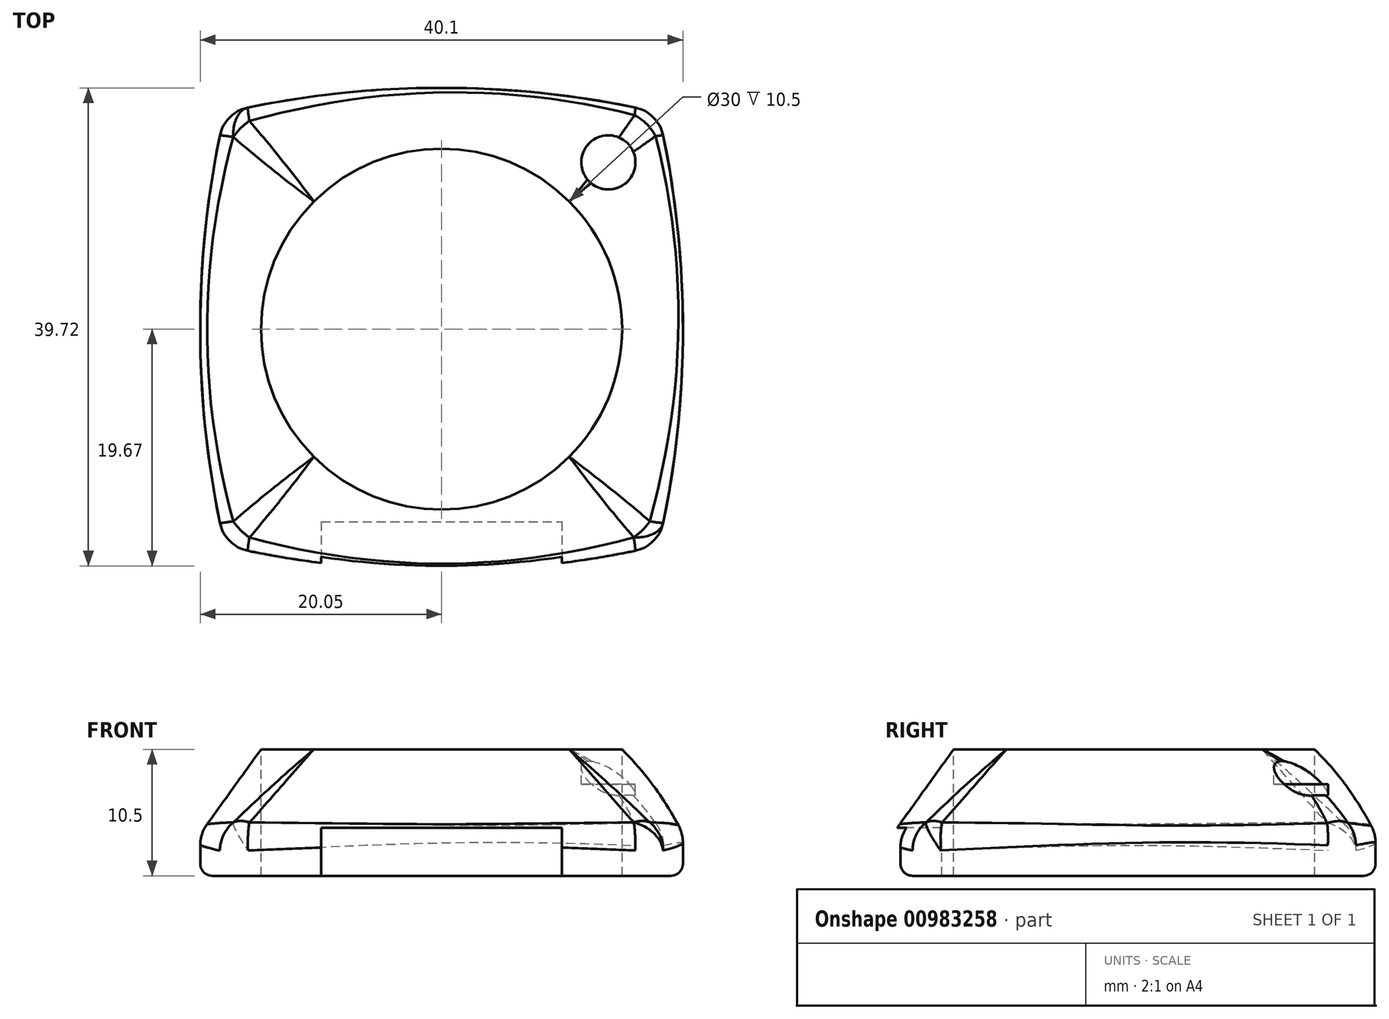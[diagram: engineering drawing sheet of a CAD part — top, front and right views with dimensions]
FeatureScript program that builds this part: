
annotation { "Feature Type Name" : "Feature", "Feature Type Description" : "" }
export const myFeature = defineFeature(function(context is Context, id is Id, definition is map)
    precondition{}
    {
        {
            assignVariable(context, id + "F0", {"name" : "base", "anyValue" : .333});
        }
        {
            assignVariable(context, id + "F1", {"name" : "Height", "anyValue" : 10.5});
        }
        {
            assignVariable(context, id + "F2", {"name" : "depth", "anyValue" : 2.9});
        }
        {
            var Q0;
            Q0=qCreatedBy(makeId("Top.planeOp"),FACE);
            var sketch = newSketch(context, id + "F3", { "sketchPlane" : qUnion([Q0])});
            skLineSegment(sketch, "E0.bottom", {"start": v(18, 18) * mm, "end": v(-18, 18) * mm});
            skLineSegment(sketch, "E0.top", {"start": v(18, -18) * mm, "end": v(-18, -18) * mm});
            skLineSegment(sketch, "E0.left", {"start": v(18, 18) * mm, "end": v(18, -18) * mm});
            skLineSegment(sketch, "E0.right", {"start": v(-18, 18) * mm, "end": v(-18, -18) * mm});
            skPoint(sketch, "E0.middle", {"position": v(0, 0) * mm});
            skArc(sketch, "E1", {"start": v(-18, 18) * mm, "mid": v(-20.05, 0) * mm, "end": v(-18, -18) * mm});
            skArc(sketch, "E2", {"start": v(18, 18) * mm, "mid": v(0, 20.05) * mm, "end": v(-18, 18) * mm});
            skArc(sketch, "E3.MirrorCS", {"start": v(18, -18) * mm, "mid": v(0, -20.05) * mm, "end": v(-18, -18) * mm});
            skArc(sketch, "E4.MirrorCS", {"start": v(18, 18) * mm, "mid": v(20.05, 0) * mm, "end": v(18, -18) * mm});
            skLineSegment(sketch, "E5", {"start": v(-18, 18) * mm, "end": v(18, -18) * mm, "construction": true});
            skLineSegment(sketch, "E6", {"start": v(18, 18) * mm, "end": v(-18, -18) * mm, "construction": true});
            skPoint(sketch, "E7", {"position": v(20.05, 0) * mm});
            skPoint(sketch, "E8", {"position": v(-20.05, 0) * mm});
            skSolve(sketch);
        }
        {
            var Q0;
            Q0=qCreatedBy(makeId("Top.planeOp"),FACE);
            cPlane(context, id + "F4", {"entities" : qUnion([Q0]), "cplaneType" : CPlaneType.OFFSET, "offset" : ((1 - getVariable(context, 'base')) * getVariable(context, 'Height')) * mm, "width" : 150 * mm, "height" : 150 * mm});
        }
        {
            var Q0;
            Q0=qSketchRegion(id+"F3",true);
            extrude(context, id + "F5", {"entities" : qUnion([Q0]), "oppositeDirection" : true, "depth" : (getVariable(context, 'base') * getVariable(context, 'Height')) * mm, "offsetDistance" : 25 * mm});
        }
        {
            var Q0;
            Q0=qCreatedBy(id+"F4.planeOp",FACE);
            var sketch = newSketch(context, id + "F6", { "sketchPlane" : qUnion([Q0])});
            skCircle(sketch, "E9", {"center": v(0, 0) * mm, "radius": 15 * mm});
            skPoint(sketch, "E10", {"position": v(15, 0) * mm});
            skPoint(sketch, "E11.1.0", {"position": v(10.6, 10.6) * mm});
            skPoint(sketch, "E11.2.0", {"position": v(0, 15) * mm});
            skPoint(sketch, "E11.3.0", {"position": v(-10.6, 10.6) * mm});
            skPoint(sketch, "E11.4.0", {"position": v(-15, 0) * mm});
            skPoint(sketch, "E11.5.0", {"position": v(-10.6, -10.6) * mm});
            skPoint(sketch, "E11.6.0", {"position": v(0, -15) * mm});
            skPoint(sketch, "E11.7.0", {"position": v(10.6, -10.6) * mm});
            skSolve(sketch);
        }
        {
            var Q0;
            Q0=makeQuery(id+"F5.opExtrude","SWEPT_EDGE",EDGE,{"disambiguationData":[OSD([sQuery(id+"F3.wireOp",EDGE,"E0.bottom"),sQuery(id+"F3.wireOp",EDGE,"E0.left"),sQuery(id+"F3.wireOp",EDGE,"E2"),sQuery(id+"F3.wireOp",EDGE,"E4.MirrorCS")])]});
            var Q1;
            Q1=sQuery(id+"F3.wireOp",VERTEX,"E0.middle");
            cPlane(context, id + "F7", {"entities" : qUnion([Q0, Q1]), "cplaneType" : CPlaneType.LINE_ANGLE, "offset" : 25 * mm, "angle" : 0 * degree, "oppositeDirection" : true, "width" : 150 * mm, "height" : 150 * mm});
        }
        {
            var Q0;
            Q0=qCreatedBy(id+"F7.planeOp",FACE);
            var sketch = newSketch(context, id + "F8", { "sketchPlane" : qUnion([Q0])});
            skArc(sketch, "E12", {"start": v(25.46, 0) * mm, "mid": v(20.68, 4.17) * mm, "end": v(15, 7) * mm});
            skLineSegment(sketch, "E13", {"start": v(0, 7.12) * mm, "end": v(0, 17.1) * mm});
            skSolve(sketch);
        }
        {
            var Q0;
            Q0=makeQuery(id+"F6.imprint","IMPRINT",FACE,{"disambiguationData":[TD([[makeQuery(id+"F6.imprint","IMPRINT",EDGE,{"derivedFrom":sQuery(id+"F6.wireOp",EDGE,"E9")}),1.0]])]});
            var Q1;
            Q1=makeQuery(id+"F5.opExtrude","CAP_FACE",FACE,{"disambiguationData":[OSD([sQuery(id+"F3.wireOp",EDGE,"E1"),sQuery(id+"F3.wireOp",EDGE,"E2"),sQuery(id+"F3.wireOp",EDGE,"E3.MirrorCS"),sQuery(id+"F3.wireOp",EDGE,"E4.MirrorCS")])],"isStart":true});
            var Q2;
            Q2=sQuery(id+"FI9qdWhZOXyrW1U_1.1.F8.wireOp",EDGE,"E12");
            var Q3;
            Q3=sQuery(id+"FI9qdWhZOXyrW1U_1.2.F8.wireOp",EDGE,"E12");
            var Q4;
            Q4=sQuery(id+"FI9qdWhZOXyrW1U_1.3.F8.wireOp",EDGE,"E12");
            var Q5;
            Q5=sQuery(id+"F8.wireOp",EDGE,"E12");
            loft(context, id + "F9", {"operationType" : NewBodyOperationType.ADD, "addGuides" : true, "sheetProfilesArray" : [{ "sheetProfileEntities" : qUnion([Q0]) }, { "sheetProfileEntities" : qUnion([Q1]) }], "guidesArray" : [{ "guideEntities" : qUnion([Q2]), "guideDerivativeType" : LoftGuideDerivativeType.DEFAULT, "guideDerivativeMagnitude" : 1 }, { "guideEntities" : qUnion([Q3]), "guideDerivativeType" : LoftGuideDerivativeType.DEFAULT, "guideDerivativeMagnitude" : 1 }, { "guideEntities" : qUnion([Q4]), "guideDerivativeType" : LoftGuideDerivativeType.DEFAULT, "guideDerivativeMagnitude" : 1 }, { "guideEntities" : qUnion([Q5]), "guideDerivativeType" : LoftGuideDerivativeType.DEFAULT, "guideDerivativeMagnitude" : 1 }]});
        }
        {
            var Q0;
            {var subQ0=sQuery(id+"F3.wireOp",EDGE,"E3.MirrorCS");Q0=makeQuery(id+"F9.boolean.opBoolean","MERGE",EDGE,{"derivedFrom":[makeQuery(id+"F5.opExtrude","CAP_EDGE",EDGE,{"disambiguationData":[OSD([subQ0])],"isStart":true}),makeQuery(id+"F9.opLoft","MID_CAP_EDGE",EDGE,{"disambiguationData":[OSD([sQuery(id+"F3.wireOp",EDGE,"E0.top"),sQuery(id+"F3.wireOp",EDGE,"E0.left"),sQuery(id+"F3.wireOp",EDGE,"E0.right"),sQuery(id+"F3.wireOp",EDGE,"E1"),subQ0,sQuery(id+"F3.wireOp",EDGE,"E4.MirrorCS")])],"capPos":1.0})]});}
            var Q1;
            {var subQ0=sQuery(id+"F3.wireOp",EDGE,"E4.MirrorCS");Q1=makeQuery(id+"F9.boolean.opBoolean","MERGE",EDGE,{"derivedFrom":[makeQuery(id+"F5.opExtrude","CAP_EDGE",EDGE,{"disambiguationData":[OSD([subQ0])],"isStart":true}),makeQuery(id+"F9.opLoft","MID_CAP_EDGE",EDGE,{"disambiguationData":[OSD([sQuery(id+"F3.wireOp",EDGE,"E0.bottom"),sQuery(id+"F3.wireOp",EDGE,"E0.top"),sQuery(id+"F3.wireOp",EDGE,"E0.left"),sQuery(id+"F3.wireOp",EDGE,"E2"),sQuery(id+"F3.wireOp",EDGE,"E3.MirrorCS"),subQ0])],"capPos":1.0})]});}
            var Q2;
            {var subQ0=sQuery(id+"F3.wireOp",EDGE,"E2");Q2=makeQuery(id+"F9.boolean.opBoolean","MERGE",EDGE,{"derivedFrom":[makeQuery(id+"F5.opExtrude","CAP_EDGE",EDGE,{"disambiguationData":[OSD([subQ0])],"isStart":true}),makeQuery(id+"F9.opLoft","MID_CAP_EDGE",EDGE,{"disambiguationData":[OSD([sQuery(id+"F3.wireOp",EDGE,"E0.bottom"),sQuery(id+"F3.wireOp",EDGE,"E0.left"),sQuery(id+"F3.wireOp",EDGE,"E0.right"),sQuery(id+"F3.wireOp",EDGE,"E1"),subQ0,sQuery(id+"F3.wireOp",EDGE,"E4.MirrorCS")])],"capPos":1.0})]});}
            var Q3;
            {var subQ0=sQuery(id+"F3.wireOp",EDGE,"E1");Q3=makeQuery(id+"F9.boolean.opBoolean","MERGE",EDGE,{"derivedFrom":[makeQuery(id+"F5.opExtrude","CAP_EDGE",EDGE,{"disambiguationData":[OSD([subQ0])],"isStart":true}),makeQuery(id+"F9.opLoft","MID_CAP_EDGE",EDGE,{"disambiguationData":[OSD([sQuery(id+"F3.wireOp",EDGE,"E0.bottom"),sQuery(id+"F3.wireOp",EDGE,"E0.top"),sQuery(id+"F3.wireOp",EDGE,"E0.right"),subQ0,sQuery(id+"F3.wireOp",EDGE,"E2"),sQuery(id+"F3.wireOp",EDGE,"E3.MirrorCS")])],"capPos":1.0})]});}
            fillet(context, id + "F10", {"entities" : qUnion([Q0, Q1, Q2, Q3]), "radius" : 3 * mm, "tangentPropagation" : true, "allowEdgeOverflow" : false});
        }
        {
            var Q0;
            Q0=makeQuery(id+"F6.imprint","IMPRINT",FACE,{"disambiguationData":[TD([[makeQuery(id+"F6.imprint","IMPRINT",EDGE,{"derivedFrom":sQuery(id+"F6.wireOp",EDGE,"E9")}),1.0]])]});
            var sketch = newSketch(context, id + "F11", { "sketchPlane" : qUnion([Q0])});
            skCircle(sketch, "E14", {"center": v(13.86, 13.86) * mm, "radius": 2.25 * mm});
            skLineSegment(sketch, "E15", {"start": v(10.6, 10.6) * mm, "end": v(13.86, 13.86) * mm, "construction": true});
            skPoint(sketch, "E16", {"position": v(10.6, 10.6) * mm});
            skSolve(sketch);
        }
        {
            var Q0;
            Q0=makeQuery(id+"F9.opLoft","SWEPT_EDGE",EDGE,{"disambiguationData":[OSD([sQuery(id+"F3.wireOp",EDGE,"E0.bottom"),sQuery(id+"F3.wireOp",EDGE,"E0.top"),sQuery(id+"F3.wireOp",EDGE,"E0.right"),sQuery(id+"F3.wireOp",EDGE,"E1"),sQuery(id+"F3.wireOp",EDGE,"E2"),sQuery(id+"F3.wireOp",EDGE,"E3.MirrorCS"),sQuery(id+"F6.wireOp",EDGE,"E9")])]});
            var Q1;
            Q1=makeQuery(id+"F9.opLoft","SWEPT_EDGE",EDGE,{"disambiguationData":[OSD([sQuery(id+"F8.wireOp",EDGE,"E12")])]});
            var Q2;
            Q2=makeQuery(id+"F9.opLoft","SWEPT_EDGE",EDGE,{"disambiguationData":[OSD([sQuery(id+"F3.wireOp",EDGE,"E0.top"),sQuery(id+"F3.wireOp",EDGE,"E0.left"),sQuery(id+"F3.wireOp",EDGE,"E3.MirrorCS"),sQuery(id+"F3.wireOp",EDGE,"E4.MirrorCS"),sQuery(id+"F6.wireOp",EDGE,"E9"),sQuery(id+"F8.wireOp",EDGE,"E12")])]});
            var Q3;
            Q3=makeQuery(id+"F9.opLoft","SWEPT_EDGE",EDGE,{"disambiguationData":[OSD([sQuery(id+"F3.wireOp",EDGE,"E0.top"),sQuery(id+"F3.wireOp",EDGE,"E0.left"),sQuery(id+"F3.wireOp",EDGE,"E0.right"),sQuery(id+"F3.wireOp",EDGE,"E1"),sQuery(id+"F3.wireOp",EDGE,"E3.MirrorCS"),sQuery(id+"F3.wireOp",EDGE,"E4.MirrorCS"),sQuery(id+"F6.wireOp",EDGE,"E9")])]});
            var Q4;
            Q4=makeQuery(id+"F9.opLoft","SWEPT_EDGE",EDGE,{"disambiguationData":[OSD([sQuery(id+"FI9qdWhZOXyrW1U_1.1.F8.wireOp",EDGE,"E12")])]});
            var Q5;
            Q5=makeQuery(id+"F9.opLoft","SWEPT_EDGE",EDGE,{"disambiguationData":[OSD([sQuery(id+"FI9qdWhZOXyrW1U_1.2.F8.wireOp",EDGE,"E12")])]});
            var Q6;
            Q6=makeQuery(id+"F9.opLoft","SWEPT_EDGE",EDGE,{"disambiguationData":[OSD([sQuery(id+"FI9qdWhZOXyrW1U_1.3.F8.wireOp",EDGE,"E12")])]});
            fillet(context, id + "F12", {"entities" : qUnion([Q0, Q1, Q2, Q3, Q4, Q5, Q6]), "radius" : 3 * mm, "tangentPropagation" : true, "allowEdgeOverflow" : false});
        }
        {
            var Q0;
            Q0=makeQuery(id+"F11.imprint","IMPRINT",FACE,{"disambiguationData":[TD([[makeQuery(id+"F11.imprint","IMPRINT",EDGE,{"derivedFrom":sQuery(id+"F11.wireOp",EDGE,"E14")}),1.0]])]});
            extrude(context, id + "F13", {"entities" : qUnion([Q0]), "operationType" : NewBodyOperationType.REMOVE, "oppositeDirection" : true, "depth" : (getVariable(context, 'depth')) * mm, "offsetDistance" : 25 * mm});
        }
        {
            var Q0;
            Q0=makeQuery(id+"F13.boolean.opBoolean","COPY",FACE,{"derivedFrom":makeQuery(id+"F13.opExtrude","CAP_FACE",FACE,{"disambiguationData":[OSD([sQuery(id+"F11.wireOp",EDGE,"E14")])],"isStart":false})});
            var sketch = newSketch(context, id + "F14", { "sketchPlane" : qUnion([Q0])});
            skCircle(sketch, "E17", {"center": v(13.86, 13.86) * mm, "radius": 2.25 * mm});
            skSolve(sketch);
        }
        {
            var Q0;
            Q0=qSketchRegion(id+"F14",true);
            extrude(context, id + "F15", {"entities" : qUnion([Q0]), "operationType" : NewBodyOperationType.ADD, "oppositeDirection" : true, "depth" : 5 * mm, "offsetDistance" : 25 * mm});
        }
        {
            var Q0;
            Q0=makeQuery(id+"F11.imprint","IMPRINT",FACE,{"disambiguationData":[TD([[makeQuery(id+"F11.imprint","IMPRINT",EDGE,{"derivedFrom":makeQuery(id+"F6.imprint","IMPRINT",EDGE,{"derivedFrom":sQuery(id+"F6.wireOp",EDGE,"E9")})}),1.0]])]});
            extrude(context, id + "F16", {"entities" : qUnion([Q0]), "operationType" : NewBodyOperationType.REMOVE, "oppositeDirection" : true, "depth" : 25 * mm, "offsetDistance" : 25 * mm});
        }
        {
            var Q0;
            Q0=makeQuery(id+"F5.opExtrude","CAP_EDGE",EDGE,{"disambiguationData":[OSD([sQuery(id+"F3.wireOp",EDGE,"E2")])],"isStart":false});
            fillet(context, id + "F17", {"entities" : qUnion([Q0]), "radius" : 1 * mm, "tangentPropagation" : true, "allowEdgeOverflow" : false});
        }
        {
            var Q0;
            Q0=qCreatedBy(makeId("Front.planeOp"),FACE);
            cPlane(context, id + "F18", {"entities" : qUnion([Q0]), "cplaneType" : CPlaneType.OFFSET, "offset" : 15.5 * mm, "width" : 150 * mm, "height" : 150 * mm});
        }
        {
            var Q0;
            Q0=qCreatedBy(id+"F18.planeOp",FACE);
            var sketch = newSketch(context, id + "F19", { "sketchPlane" : qUnion([Q0])});
            skLineSegment(sketch, "E18.right", {"start": v(-9, -3.5) * mm, "end": v(-9, 2.16) * mm});
            skCircle(sketch, "E19", {"center": v(-11.5, -0.9) * mm, "radius": 1.5 * mm});
            skLineSegment(sketch, "E20", {"start": v(0, 0) * mm, "end": v(0, -1.75) * mm, "construction": true});
            skLineSegment(sketch, "E21", {"start": v(0, -1.75) * mm, "end": v(0, -3.64) * mm, "construction": true});
            skLineSegment(sketch, "E22", {"start": v(-11.5, -0.9) * mm, "end": v(-10, -0.9) * mm, "construction": true});
            skSolve(sketch);
        }
        {
            var Q0;
            Q0=sQuery(id+"F19.wireOp",VERTEX,"E19.center");
            var Q1;
            Q1=sQuery(id+"F19.wireOp",EDGE,"E18.right");
            cPlane(context, id + "F20", {"entities" : qUnion([Q0, Q1]), "cplaneType" : CPlaneType.LINE_POINT, "offset" : 25 * mm, "width" : 150 * mm, "height" : 150 * mm});
        }
        {
            assignVariable(context, id + "F21", {"name" : "lug", "anyValue" : 20 * mm});
        }
        {
            var Q0;
            Q0=qCreatedBy(makeId("Right.planeOp"),FACE);
            cPlane(context, id + "F22", {"entities" : qUnion([Q0]), "cplaneType" : CPlaneType.OFFSET, "offset" : getVariable(context, 'lug') / 2, "width" : 150 * mm, "height" : 150 * mm});
        }
        {
            var Q0;
            Q0=qCreatedBy(id+"F22.planeOp",FACE);
            var sketch = newSketch(context, id + "F23", { "sketchPlane" : qUnion([Q0])});
            skLineSegment(sketch, "E23.bottom", {"start": v(-16, -3.5) * mm, "end": v(-20.88, -3.5) * mm});
            skLineSegment(sketch, "E23.top", {"start": v(-16, 0.5) * mm, "end": v(-20.88, 0.5) * mm});
            skLineSegment(sketch, "E23.left", {"start": v(-16, -3.5) * mm, "end": v(-16, 0.5) * mm});
            skLineSegment(sketch, "E23.right", {"start": v(-20.88, -3.5) * mm, "end": v(-20.88, 0.5) * mm});
            skSolve(sketch);
        }
        {
            var Q0;
            Q0 = qSketchRegion(id + "F23", true);
            extrude(context, id + "F24", {"entities" : qUnion([Q0]), "operationType" : NewBodyOperationType.REMOVE, "oppositeDirection" : true, "depth" : getVariable(context, 'lug'), "offsetDistance" : 25 * mm});
        }
    });
